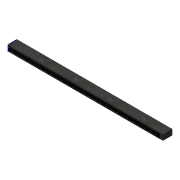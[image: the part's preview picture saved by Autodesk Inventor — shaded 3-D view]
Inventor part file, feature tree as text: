
AUTODESK INVENTOR PART (.ipt)
format: ipt  version: 2016 (Build 200138000, 138)  size: 401,920 bytes
history: native  units: mm
features: sketch x6, extrude x5, projected_geometry x1
ambient origin geometry x8: Origin, YZ Plane, XZ Plane, XY Plane, X Axis, Y Axis, Z Axis, Center Point
bodies: Solid1 (feature_tree), Solid2 (feature_tree)
feature tree (12):
  extrude  "Extrusion1"  Depth=30.0mm
  extrude  "Extrusion2"  Depth=12.5mm
  extrude  "Extrusion3"  Depth=7.0mm
  extrude  "Extrusion4"  Depth=17.0mm
  extrude  "Extrusion5"  Depth=23.0mm
  sketch  "Sketch8"  dims[d14=5.0mm d15=5.0mm d16=23.0mm d17=5.0mm d18=5.0mm d19=23.0mm d20=5.0mm d21=5.0mm d22=23.0mm d23=5.0mm d24=5.0mm d25=23.0mm d26=5.0mm d27=5.0mm d28=23.0mm d29=5.0mm d30=5.0mm d31=2.5mm d33=0.0mm d34=0.0mm d37=1.0mm d38=779.45mm d39=0.0mm d40=1.0mm d41=779.45mm d42=0.0mm]
  sketch  "Sketch1"  dims[d0=47.0mm d1=30.0mm]
  sketch  "Sketch2"  dims[d2=794.45mm d3=0.0mm d4=12.5mm]
  sketch  "Sketch3"  dims[d5=37.0mm d6=7.0mm]
  sketch  "Sketch5"  dims[d9=5.0mm d10=17.0mm]
  sketch  "Sketch6"  dims[d11=779.45mm d12=0.0mm d13=23.0mm]
  projected_geometry  "Projected Loop1"
